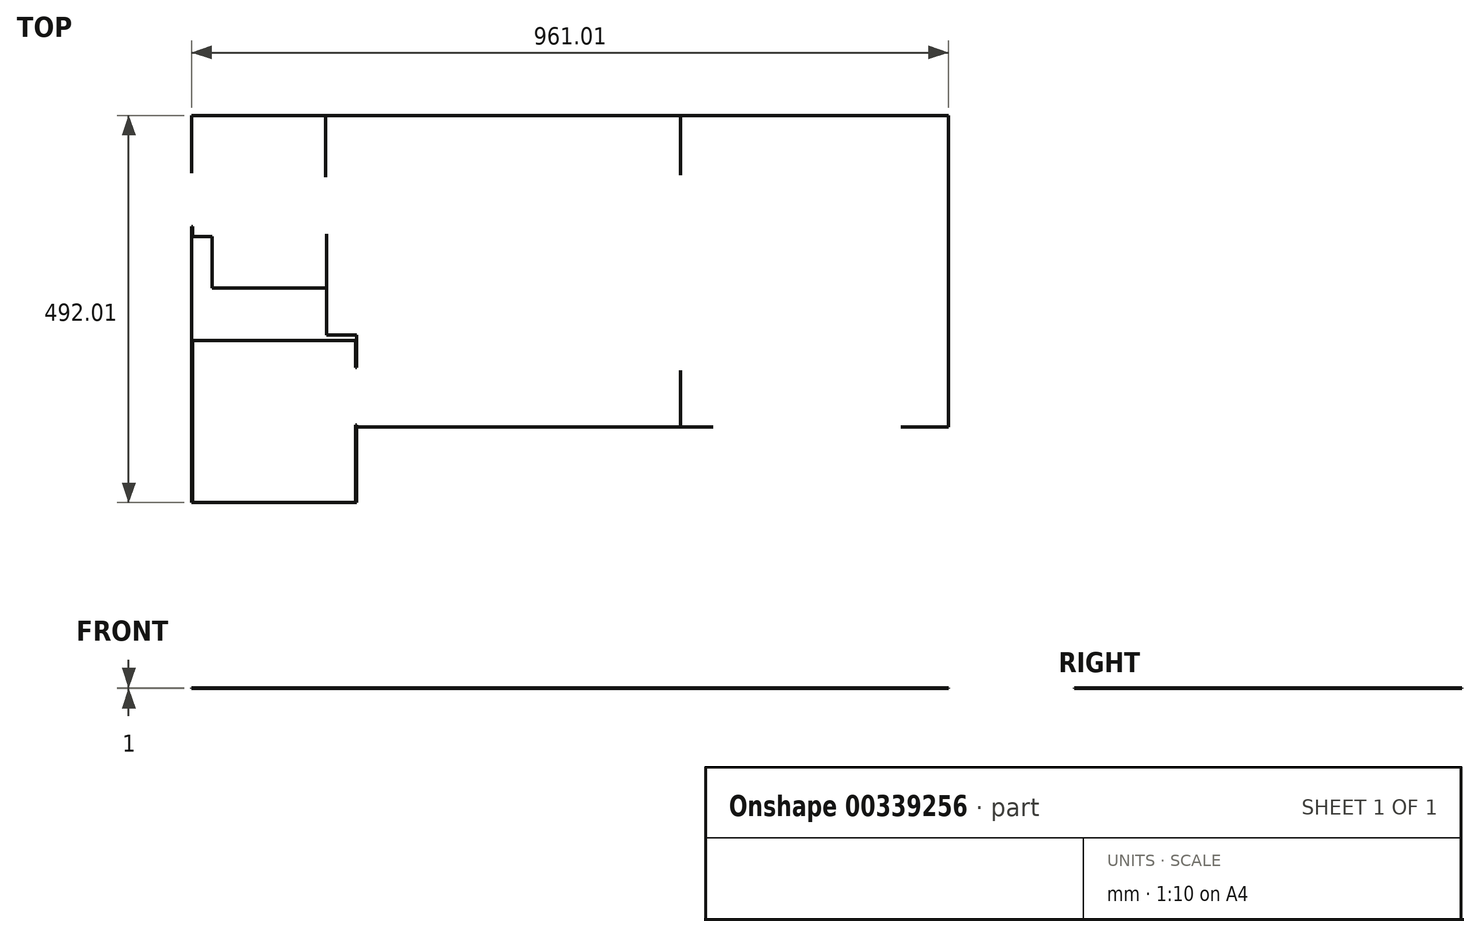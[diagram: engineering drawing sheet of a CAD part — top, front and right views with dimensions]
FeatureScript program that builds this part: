
annotation { "Feature Type Name" : "Feature", "Feature Type Description" : "" }
export const myFeature = defineFeature(function(context is Context, id is Id, definition is map)
    precondition{}
    {
        {
            var Q0;
            Q0=qCreatedBy(makeId("Top.planeOp"),FACE);
            var sketch = newSketch(context, id + "F0", { "sketchPlane" : qUnion([Q0])});
            skLineSegment(sketch, "E0.bottom", {"start": v(104.22, 11) * mm, "end": v(-307.78, 11) * mm});
            skLineSegment(sketch, "E0.top", {"start": v(104.22, 407) * mm, "end": v(-346.76, 407) * mm});
            skLineSegment(sketch, "E1.left", {"start": v(-346.76, 407) * mm, "end": v(-346.76, 384.44) * mm});
            skLineSegment(sketch, "E2.0", {"start": v(104.23, 407) * mm, "end": v(-346.77, 407) * mm});
            skLineSegment(sketch, "E3.0", {"start": v(104.23, 11) * mm, "end": v(104.23, 83) * mm});
            skLineSegment(sketch, "E4.0", {"start": v(104.23, 11) * mm, "end": v(-307.78, 10.99) * mm});
            skLineSegment(sketch, "E5", {"start": v(-307.78, 128) * mm, "end": v(-307.78, 87) * mm});
            skLineSegment(sketch, "E6", {"start": v(-307.78, 128) * mm, "end": v(-345.77, 128) * mm});
            skLineSegment(sketch, "E7.trimOffspring", {"start": v(-307.78, 10.99) * mm, "end": v(-307.78, -85) * mm});
            skLineSegment(sketch, "E8", {"start": v(-308.78, 87) * mm, "end": v(-307.78, 87) * mm});
            skLineSegment(sketch, "E9.trimOffspring", {"start": v(-308.78, 14) * mm, "end": v(-308.78, -85) * mm});
            skLineSegment(sketch, "E10", {"start": v(-307.78, -85) * mm, "end": v(-308.78, -85) * mm});
            skLineSegment(sketch, "E11", {"start": v(104.22, 83) * mm, "end": v(104.23, 83) * mm});
            skLineSegment(sketch, "E12", {"start": v(104.22, 331) * mm, "end": v(104.23, 331) * mm});
            skLineSegment(sketch, "E13.trimOffspring", {"start": v(104.23, 331) * mm, "end": v(104.23, 407) * mm});
            skLineSegment(sketch, "E14.trimOffspring", {"start": v(104.22, 331) * mm, "end": v(104.22, 407) * mm});
            skLineSegment(sketch, "E15.trimOffspring", {"start": v(104.22, 11) * mm, "end": v(104.22, 83) * mm});
            skLineSegment(sketch, "E16", {"start": v(104.23, 11) * mm, "end": v(145.23, 11) * mm});
            skLineSegment(sketch, "E17", {"start": v(145.23, 11) * mm, "end": v(145.23, 10.99) * mm});
            skLineSegment(sketch, "E18", {"start": v(414.22, 0) * mm, "end": v(414.22, -1) * mm});
            skPoint(sketch, "E19.orphan", {"position": v(58.62, 0) * mm});
            skLineSegment(sketch, "E20", {"start": v(-346.77, 329) * mm, "end": v(-346.76, 329) * mm});
            skLineSegment(sketch, "E21", {"start": v(-345.78, 256) * mm, "end": v(-345.77, 256) * mm});
            skLineSegment(sketch, "E22.trimOffspring", {"start": v(-346.76, 329) * mm, "end": v(-346.76, 407) * mm});
            skLineSegment(sketch, "E23.trimOffspring", {"start": v(-346.77, 329) * mm, "end": v(-346.77, 407) * mm});
            skLineSegment(sketch, "E24", {"start": v(-346.77, 407) * mm, "end": v(-516.78, 407) * mm});
            skLineSegment(sketch, "E25", {"start": v(-346.77, 407) * mm, "end": v(-516.77, 407) * mm});
            skLineSegment(sketch, "E26", {"start": v(-516.78, 407) * mm, "end": v(-516.78, 334) * mm});
            skLineSegment(sketch, "E27.0", {"start": v(-516.77, 407) * mm, "end": v(-516.77, 334) * mm});
            skPoint(sketch, "E28.orphan", {"position": v(-516.78, 407) * mm});
            skLineSegment(sketch, "E29", {"start": v(-516.78, 334) * mm, "end": v(-516.77, 334) * mm});
            skLineSegment(sketch, "E30", {"start": v(-516.78, 240.87) * mm, "end": v(-516.78, 240.87) * mm});
            skLineSegment(sketch, "E31", {"start": v(-515.78, 266) * mm, "end": v(-515.78, 253) * mm});
            skLineSegment(sketch, "E32", {"start": v(-515.78, 253) * mm, "end": v(-490.78, 253) * mm});
            skPoint(sketch, "E33.orphan", {"position": v(-516.78, 253) * mm});
            skLineSegment(sketch, "E34", {"start": v(-516.78, 266) * mm, "end": v(-515.78, 266) * mm});
            skLineSegment(sketch, "E35.trimOffspring", {"start": v(-516.78, 266) * mm, "end": v(-516.78, 252) * mm});
            skLineSegment(sketch, "E36", {"start": v(-490.78, 253) * mm, "end": v(-490.78, 188) * mm});
            skLineSegment(sketch, "E37.trimOffspring", {"start": v(-490.78, 188) * mm, "end": v(-345.78, 188) * mm});
            skLineSegment(sketch, "E38.trimOffspring", {"start": v(-345.78, 188) * mm, "end": v(-345.78, 256) * mm});
            skLineSegment(sketch, "E39", {"start": v(104.23, 407.01) * mm, "end": v(445.2, 407.01) * mm});
            skLineSegment(sketch, "E40", {"start": v(104.23, 407) * mm, "end": v(445.26, 407) * mm});
            skLineSegment(sketch, "E41.0", {"start": v(444.22, 11) * mm, "end": v(444.22, 410) * mm});
            skLineSegment(sketch, "E42", {"start": v(384.23, 11) * mm, "end": v(444.23, 11) * mm});
            skLineSegment(sketch, "E43.0", {"start": v(384.23, 11) * mm, "end": v(444.22, 11) * mm});
            skLineSegment(sketch, "E44", {"start": v(384.23, 11) * mm, "end": v(384.23, 11) * mm});
            skPoint(sketch, "E45.orphan", {"position": v(341.53, 11) * mm});
            skLineSegment(sketch, "E46.trimOffspring", {"start": v(444.23, 11) * mm, "end": v(444.23, 407.01) * mm});
            skLineSegment(sketch, "E47", {"start": v(-307.78, -85) * mm, "end": v(-516.78, -85) * mm});
            skLineSegment(sketch, "E48.0", {"start": v(-308.78, -85) * mm, "end": v(-515.78, -85) * mm});
            skLineSegment(sketch, "E49.0", {"start": v(-516.78, 233) * mm, "end": v(-516.78, -85) * mm});
            skLineSegment(sketch, "E50", {"start": v(-307.78, 11) * mm, "end": v(-307.78, 14) * mm});
            skLineSegment(sketch, "E51", {"start": v(-308.78, 14) * mm, "end": v(-307.78, 14) * mm});
            skLineSegment(sketch, "E52", {"start": v(-308.78, 121) * mm, "end": v(-345.78, 121) * mm});
            skLineSegment(sketch, "E53.trimOffspring", {"start": v(-308.78, 121) * mm, "end": v(-308.78, 87) * mm});
            skLineSegment(sketch, "E54.trimOffspring", {"start": v(-345.77, 128) * mm, "end": v(-345.77, 256) * mm});
            skLineSegment(sketch, "E55", {"start": v(-516.78, 252) * mm, "end": v(-516.78, 233) * mm});
            skLineSegment(sketch, "E56", {"start": v(-345.78, 121) * mm, "end": v(-515.78, 121) * mm});
            skLineSegment(sketch, "E57.trimOffspring", {"start": v(-515.78, 121) * mm, "end": v(-515.78, -85) * mm});
            skSolve(sketch);
        }
        {
            var Q0;
            Q0 = qSketchRegion(id + "F0", true);
            extrude(context, id + "F1", {"entities" : qUnion([Q0]), "depth" : 1 * mm});
        }
    });
